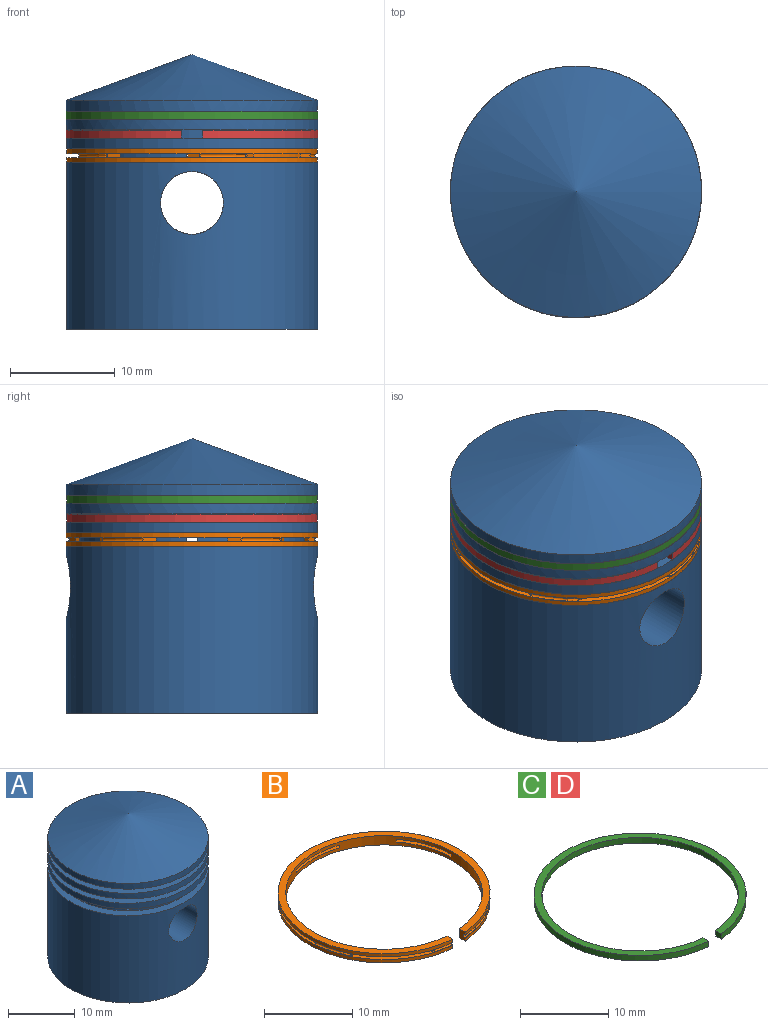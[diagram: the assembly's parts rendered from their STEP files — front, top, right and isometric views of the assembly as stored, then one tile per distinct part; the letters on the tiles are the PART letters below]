
ASSEMBLY  parts=4 mates=3
PART A: 32 faces, bbox 24x24x26.2 mm
  f0: cylinder r=4.76mm len=12.7mm, axis (0,0,-1), area 188.4mm2, adj f6,f7,f8,f9,f26,f27,f28
  f1: cylinder r=4.76mm len=12.7mm, axis (0,0,-1), area 188.4mm2, adj f6,f7,f8,f9,f23,f24,f25
  f2: cylinder r=10.72mm len=21.44mm, axis (0,0,1), area 78.9mm2, adj f10,f11,f22,f23,f24,f25,f26,f27
  f3: cylinder r=11.98mm len=23.97mm, axis (0,0,1), area 1144.1mm2, adj f4,f11,f30,f31
  f4: plane 23.97x23.97mm, normal (0,0,-1), area 63.1mm2, adj f3,f5
  f5: cylinder r=11.11mm len=22.23mm, axis (0,0,-1), area 532mm2, adj f4,f6
  f6: plane 22.23x22.23mm, normal (0,0,-1), area 219.9mm2, adj f0,f1,f5,f8,f9
  f7: plane 19.69x9.53mm, normal (0,0,-1), area 168mm2, adj f0,f1,f8,f9
  f8: plane 12.71x10.17mm, normal (0,1,0), area 97.9mm2, adj f0,f1,f6,f7,f22,f23,f26,f31
  f9: plane 12.71x10.17mm, normal (0,-1,0), area 97.9mm2, adj f0,f1,f6,f7,f25,f28,f29,f30
  f10: plane 23.97x23.97mm, normal (0,0,-1), area 90.1mm2, adj f2,f12
  f11: plane 23.97x23.97mm, normal (0,0,1), area 90.1mm2, adj f2,f3
  f12: cylinder r=11.98mm len=23.97mm, axis (0,0,1), area 75.5mm2, adj f10,f14
  f13: plane 23.97x23.97mm, normal (0,0,-1), area 90.1mm2, adj f15,f16
  f14: plane 23.97x23.97mm, normal (0,0,1), area 90.1mm2, adj f12,f15
  f15: cylinder r=10.72mm len=21.44mm, axis (0,0,1), area 53mm2, adj f13,f14
  f16: cylinder r=11.98mm len=23.97mm, axis (0,0,1), area 76.5mm2, adj f13,f18
  f17: plane 23.97x23.97mm, normal (0,0,-1), area 90.1mm2, adj f19,f21
  f18: plane 23.97x23.97mm, normal (0,0,1), area 90.1mm2, adj f16,f19
  f19: cylinder r=10.72mm len=21.44mm, axis (0,0,1), area 53mm2, adj f17,f18
  f20: cone r=11.98mm half-angle=70deg, axis (0,0,-1), area 480mm2, adj f21
  f21: cylinder r=11.98mm len=23.97mm, axis (0,0,1), area 77.1mm2, adj f17,f20
  f22: cylinder r=0.55mm len=5.96mm, axis (0,1,0), area 20.4mm2, adj f2,f8
  f23: cylinder r=0.55mm len=3.98mm, axis (-0.71,-0.71,0), area 13.7mm2, adj f1,f2,f8
  f24: cylinder r=0.55mm len=1.09mm, axis (-1,0,0), area 3.1mm2, adj f1,f2
  f25: cylinder r=0.55mm len=3.98mm, axis (-0.71,0.71,0), area 13.7mm2, adj f1,f2,f9
  f26: cylinder r=0.55mm len=3.98mm, axis (-0.71,0.71,0), area 13.7mm2, adj f0,f2,f8
  f27: cylinder r=0.55mm len=1.09mm, axis (-1,0,0), area 3.1mm2, adj f0,f2
  f28: cylinder r=0.55mm len=3.98mm, axis (-0.71,-0.71,0), area 13.7mm2, adj f0,f2,f9
  f29: cylinder r=0.55mm len=5.96mm, axis (0,1,0), area 20.4mm2, adj f2,f9
  f30: cylinder r=3mm len=7.22mm, axis (0,-1,0), area 132.4mm2, adj f3,f9
  f31: cylinder r=3mm len=7.22mm, axis (0,-1,0), area 132.4mm2, adj f3,f8
PART B: 26 faces, bbox 26.1x24.1x1.3 mm
  f0: cylinder r=11.99mm len=23.98mm, axis (0,0,-1), area 32.6mm2, adj f1,f2,f3,f4
  f1: plane 1.27x0.88mm, normal (1,0,0), area 1mm2, adj f0,f2,f4,f5,f6,f7,f8,f9
  f2: plane 23.98x23.93mm, normal (0,0,1), area 40mm2, adj f0,f1,f3,f6,f7,f10,f11,f12
  f3: plane 1.27x0.88mm, normal (-1,0,0), area 1mm2, adj f0,f2,f4,f5,f7,f8,f9,f11
  f4: plane 23.98x23.93mm, normal (0,0,-1), area 61.8mm2, adj f0,f1,f3,f7
  f5: plane 23.98x23.93mm, normal (0,0,-1), area 40mm2, adj f1,f3,f6,f7,f9,f10,f11,f12
  f6: torus R=11.93mm, axis (0,0,-1), area 1.4mm2, adj f1,f2,f5,f12
  f7: cylinder r=11.11mm len=22.23mm, axis (0,0,-1), area 75.5mm2, adj f1,f2,f3,f4,f5,f8,f10,f16
  f8: plane 23.98x23.93mm, normal (0,0,1), area 61.8mm2, adj f1,f3,f7,f9
  f9: cylinder r=11.99mm len=23.98mm, axis (0,0,-1), area 32.6mm2, adj f1,f3,f5,f8
  f10: cylinder r=25.4mm len=1.2mm, axis (0,0,-1), area 0.5mm2, adj f2,f5,f7,f11
  f11: torus R=11.93mm, axis (0,0,-1), area 1.4mm2, adj f2,f3,f5,f10
  f12: cylinder r=25.4mm len=1.2mm, axis (0,0,-1), area 0.5mm2, adj f2,f5,f6,f13
  f13: cylinder r=11.11mm len=5.25mm, axis (0,0,-1), area 2.7mm2, adj f2,f5,f12,f14
  f14: cylinder r=25.4mm len=1.36mm, axis (0,0,-1), area 0.5mm2, adj f2,f5,f13,f15
  f15: torus R=11.93mm, axis (0,0,-1), area 2.7mm2, adj f2,f5,f14,f16
  f16: cylinder r=25.4mm len=1.38mm, axis (0,0,-1), area 0.5mm2, adj f2,f5,f7,f15
  f17: cylinder r=25.4mm len=1.55mm, axis (0,0,-1), area 0.5mm2, adj f2,f5,f7,f18
  f18: torus R=11.93mm, axis (0,0,-1), area 2.7mm2, adj f2,f5,f17,f19
  f19: cylinder r=25.4mm len=1.56mm, axis (0,0,-1), area 0.5mm2, adj f2,f5,f7,f18
  f20: cylinder r=25.4mm len=1.56mm, axis (0,0,-1), area 0.5mm2, adj f2,f5,f7,f21
  f21: torus R=11.93mm, axis (0,0,-1), area 2.7mm2, adj f2,f5,f20,f22
  f22: cylinder r=25.4mm len=1.55mm, axis (0,0,-1), area 0.5mm2, adj f2,f5,f7,f21
  f23: cylinder r=25.4mm len=1.38mm, axis (0,0,-1), area 0.5mm2, adj f2,f5,f7,f24
  f24: torus R=11.93mm, axis (0,0,-1), area 2.7mm2, adj f2,f5,f23,f25
  f25: cylinder r=25.4mm len=1.36mm, axis (0,0,-1), area 0.5mm2, adj f2,f5,f7,f24
PART C: 6 faces, bbox 24x23.9x0.8 mm
  f0: cylinder r=11.11mm len=22.23mm, axis (0,0,-1), area 51.7mm2, adj f1,f3,f4,f5
  f1: plane 23.98x23.93mm, normal (0,0,-1), area 61.8mm2, adj f0,f2,f4,f5
  f2: cylinder r=11.99mm len=23.98mm, axis (0,0,-1), area 55.8mm2, adj f1,f3,f4,f5
  f3: plane 23.98x23.93mm, normal (0,0,1), area 61.8mm2, adj f0,f2,f4,f5
  f4: plane 0.88x0.76mm, normal (1,0,0), area 0.7mm2, adj f0,f1,f2,f3
  f5: plane 0.88x0.76mm, normal (-1,0,0), area 0.7mm2, adj f0,f1,f2,f3
PART D: same geometry as C
PLACE A at identity fixed
PLACE B rot(axis=(0,0,1),90deg) t=(0,0,15.95)mm
PLACE C rot(axis=(0,0,1),180deg) t=(0,0,20.04)mm
PLACE D t=(0,0,18.24)mm
MATE fastened D.f0 <-> A.f2  axis (0,0,-1) through (0,0,18.24)mm
MATE fastened C.f0 <-> A.f2  axis (0,0,-1) through (0,0,20.04)mm
MATE fastened B.f0 <-> A.f2  axis (0,0,-1) through (0,0,15.95)mm
